# Revit family: Data_Device-Network-Leviton-Enclosures-2000i_SDX
name_source: partatom
category: Data Devices
units: mm (PartAtom-declared; Revit-internal decimal feet)

## family parameters
Cut with Voids When Loaded = No
Host = Face
Maintain Annotation Orientation = Yes
OmniClass Number = 23.85.50.17
OmniClass Title = Communication and Data Processing Equipment
Part Type = Normal
Room Calculation Point = No
Round Connector Dimension = Use Diameter
Shared = Yes

## types (3) — shared parameters
Annotation Symbol is Visible = Yes
Assembly Code = D5030600
Date Last Modified = September 15, 2023
Default Elevation = 2' - 0"
Equipment Abbreviation = RME
Family Version = 1.0.0
Has ID Windows = No
Host Plane Offset = 0' - 0 1/2"
Manufacturer = Leviton
Model Disclaimer = http://www.leviton.com
Product Documentation Link = https://www.leviton.com
Shielded = No
URL = http://www.leviton.com

## per-type parameters (varying)
| type | Description | Part Description | Rack Spaces RU | z Is Visible 1RU | z Is Visible 2RU | z Is Visible 4RU | z Leviton Type | z Offset 1 | z Offset 2 |
| Opt-X 2000i SDX 1RU RM Enclosure, 3 Trays | 4RU Enclosure, empty, with sliding tray. | 4RU Enclosure, empty, with sliding tray. | 1 | Yes | No | No | 1 | 0' - 1 11/16" | 0' - 0 1/8" |
| Opt-X 2000i SDX 4RU RM Enclosure, 12 Trays | 4RU Enclosure, empty, with sliding tray. | 4RU Enclosure, empty, with sliding tray. | 4 | No | No | Yes | 3 | 0' - 1 3/4" | 0' - 0 3/8" |
| Opt-X 2000i SDX 2RU RM Enclosure, 6 Trays | 2RU Enclosure, empty, with sliding tray. | 2RU Enclosure, empty, with sliding tray. | 2 | No | Yes | No | 2 | 0' - 1 13/16" | 0' - 0 3/16" |

## geometry (parser evidence)
native form markers: Blend x76, Sweep x30
no freeform markers — native parametric forms only
